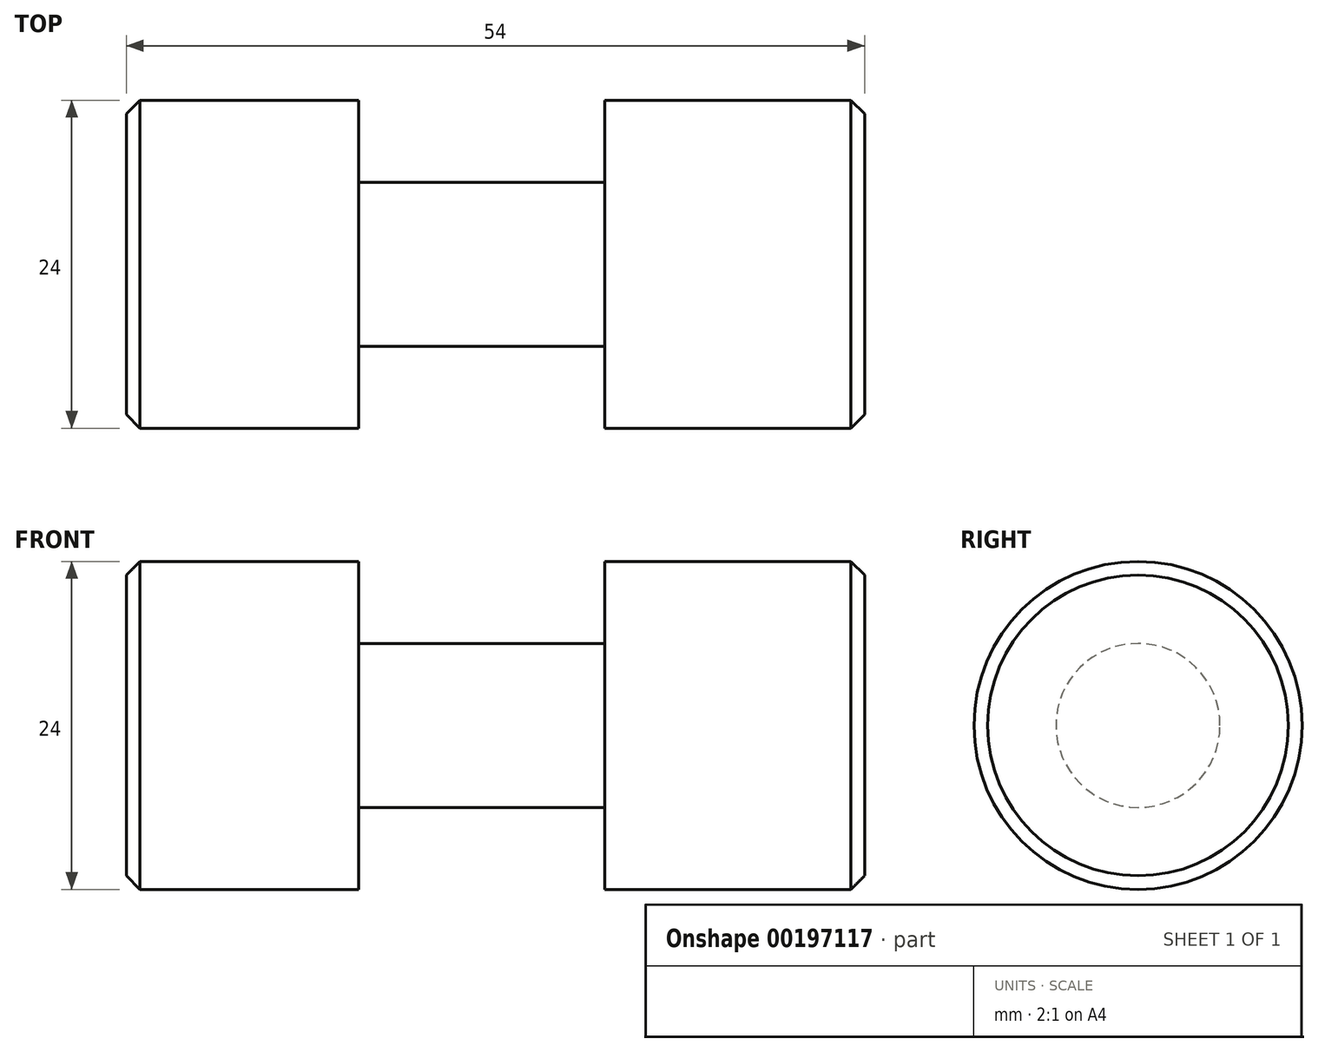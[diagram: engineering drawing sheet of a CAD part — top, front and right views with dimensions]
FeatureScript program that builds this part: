
annotation { "Feature Type Name" : "Feature", "Feature Type Description" : "" }
export const myFeature = defineFeature(function(context is Context, id is Id, definition is map)
    precondition{}
    {
        {
            var Q0;
            Q0=qCreatedBy(makeId("Front.planeOp"),FACE);
            var sketch = newSketch(context, id + "F0", { "sketchPlane" : qUnion([Q0]), "disableImprinting" : false});
            skLineSegment(sketch, "E0", {"start": v(-5.55, 0) * mm, "end": v(62.74, 0) * mm, "construction": true});
            skLineSegment(sketch, "E1", {"start": v(0, 0) * mm, "end": v(0, 12) * mm});
            skLineSegment(sketch, "E2", {"start": v(0, 12) * mm, "end": v(17, 12) * mm});
            skLineSegment(sketch, "E3", {"start": v(17, 12) * mm, "end": v(17, 6) * mm});
            skLineSegment(sketch, "E4", {"start": v(17, 6) * mm, "end": v(35, 6) * mm});
            skLineSegment(sketch, "E5", {"start": v(35, 6) * mm, "end": v(35, 12) * mm});
            skLineSegment(sketch, "E6", {"start": v(35, 12) * mm, "end": v(54, 12) * mm});
            skLineSegment(sketch, "E7", {"start": v(54, 12) * mm, "end": v(54, 0) * mm});
            skLineSegment(sketch, "E8", {"start": v(54, 0) * mm, "end": v(0, 0) * mm});
            skSolve(sketch);
        }
        {
            var Q0;
            Q0 = qSketchRegion(id + "F0", true);
            var Q1;
            Q1=sQuery(id+"F0.wireOp",EDGE,"E0");
            revolve(context, id + "F1", {"entities" : qUnion([Q0]), "axis" : qUnion([Q1]), "revolveType" : RevolveType.FULL});
        }
        {
            var Q0;
            Q0=makeQuery(id+"F1.opRevolve","SWEPT_EDGE",EDGE,{"disambiguationData":[OSD([sQuery(id+"F0.wireOp",EDGE,"E1"),sQuery(id+"F0.wireOp",EDGE,"E2")])]});
            var Q1;
            Q1=makeQuery(id+"F1.opRevolve","SWEPT_EDGE",EDGE,{"disambiguationData":[OSD([sQuery(id+"F0.wireOp",EDGE,"E6"),sQuery(id+"F0.wireOp",EDGE,"E7")])]});
            chamfer(context, id + "F2", {"entities" : qUnion([Q0, Q1]), "width" : 1 * mm, "tangentPropagation" : true});
        }
    });
